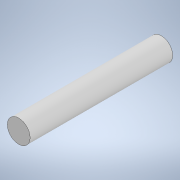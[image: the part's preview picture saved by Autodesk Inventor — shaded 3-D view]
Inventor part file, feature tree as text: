
AUTODESK INVENTOR PART (.ipt)
format: ipt  version: 2020.2 (Build 242310000, 310)  size: 89,600 bytes
history: native  units: mm
features: extrude x1, sketch x1
ambient origin geometry x8: Origin, YZ Plane, XZ Plane, XY Plane, X Axis, Y Axis, Z Axis, Center Point
bodies: Solide1 (feature_tree)
feature tree (2):
  extrude  "Extrusion1"  Depth=8.0mm
  sketch  "Esquisse1"
